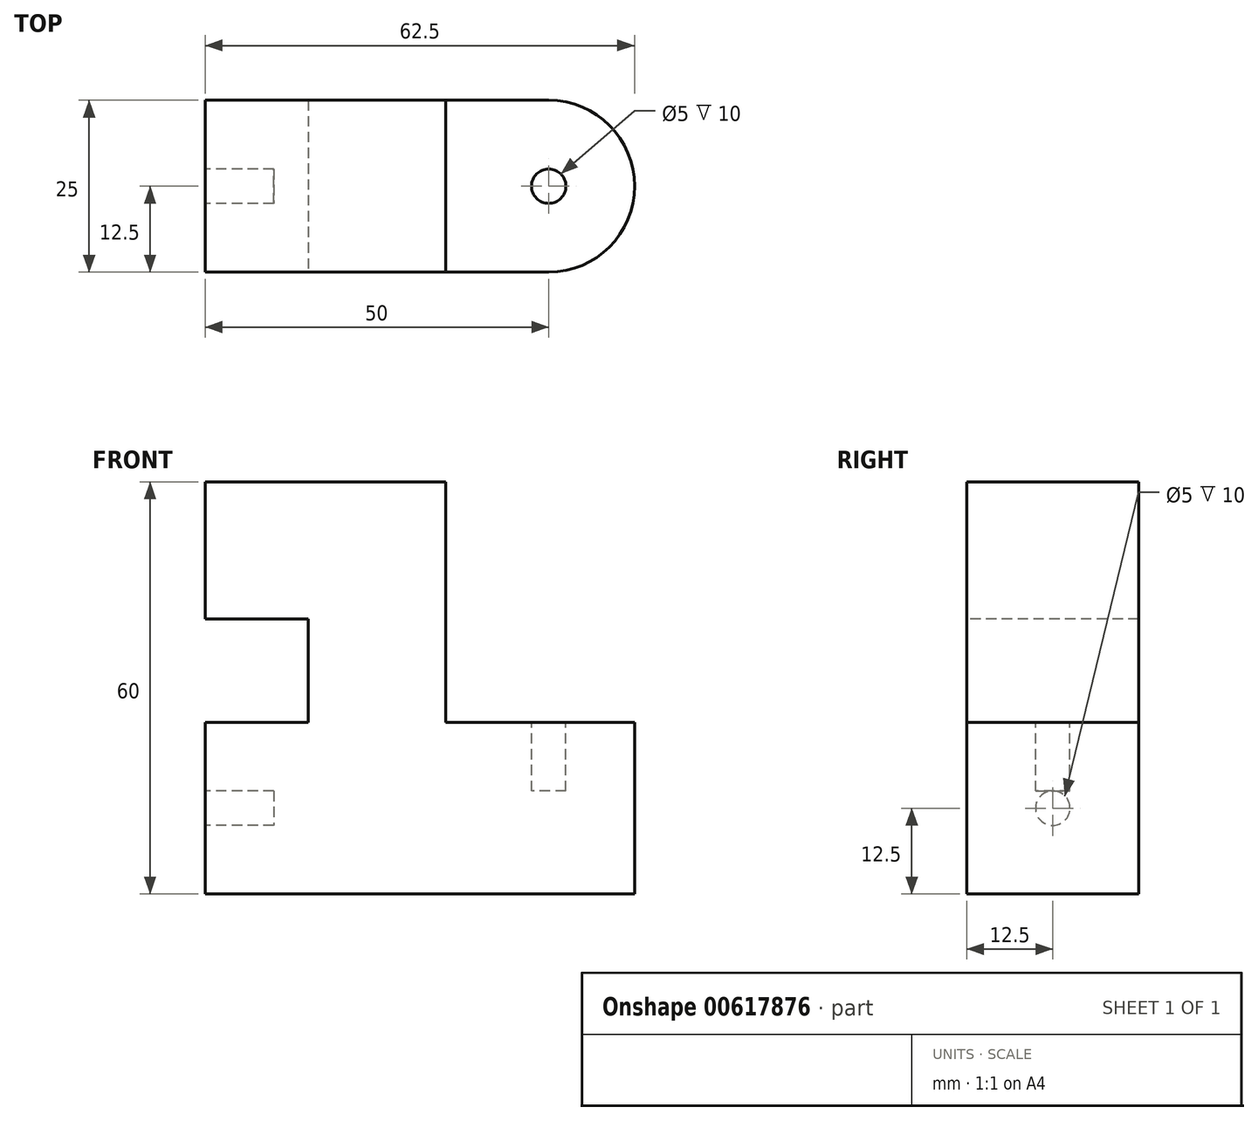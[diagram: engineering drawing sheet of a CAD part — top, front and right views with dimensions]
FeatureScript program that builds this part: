
annotation { "Feature Type Name" : "Feature", "Feature Type Description" : "" }
export const myFeature = defineFeature(function(context is Context, id is Id, definition is map)
    precondition{}
    {
        {
            var Q0;
            Q0=qCreatedBy(makeId("Top.planeOp"),FACE);
            var sketch = newSketch(context, id + "F0", { "sketchPlane" : qUnion([Q0])});
            skLineSegment(sketch, "E0.bottom", {"start": v(0, 0) * mm, "end": v(50, 0) * mm});
            skLineSegment(sketch, "E0.top", {"start": v(0, 25) * mm, "end": v(50, 25) * mm});
            skLineSegment(sketch, "E0.left", {"start": v(0, 0) * mm, "end": v(0, 25) * mm});
            skArc(sketch, "E1", {"start": v(50, 0) * mm, "mid": v(62.5, 12.5) * mm, "end": v(50, 25) * mm});
            skSolve(sketch);
        }
        {
            var Q0;
            Q0=makeQuery(id+"F0.imprint","IMPRINT",FACE,{"disambiguationData":[TD([[makeQuery(id+"F0.imprint","IMPRINT",EDGE,{"derivedFrom":sQuery(id+"F0.wireOp",EDGE,"E0.bottom")}),1.0]])]});
            extrude(context, id + "F1", {"entities" : qUnion([Q0]), "depth" : 25 * mm, "offsetDistance" : 25 * mm});
        }
        {
            var Q0;
            Q0=makeQuery(id+"F1.opExtrude","CAP_FACE",FACE,{"disambiguationData":[OSD([sQuery(id+"F0.wireOp",EDGE,"E0.bottom"),sQuery(id+"F0.wireOp",EDGE,"E0.top"),sQuery(id+"F0.wireOp",EDGE,"E0.left"),sQuery(id+"F0.wireOp",EDGE,"E1")])],"isStart":false});
            var sketch = newSketch(context, id + "F2", { "sketchPlane" : qUnion([Q0])});
            skCircle(sketch, "E2", {"center": v(50, 12.5) * mm, "radius": 2.5 * mm});
            skSolve(sketch);
        }
        {
            var Q0;
            Q0=makeQuery(id+"F2.imprint","IMPRINT",FACE,{"disambiguationData":[TD([[makeQuery(id+"F2.imprint","IMPRINT",EDGE,{"derivedFrom":sQuery(id+"F2.wireOp",EDGE,"E2")}),1.0]])]});
            extrude(context, id + "F3", {"entities" : qUnion([Q0]), "operationType" : NewBodyOperationType.REMOVE, "oppositeDirection" : true, "depth" : 10 * mm, "offsetDistance" : 25 * mm});
        }
        {
            var Q0;
            Q0=makeQuery(id+"F1.opExtrude","SWEPT_FACE",FACE,{"disambiguationData":[OSD([sQuery(id+"F0.wireOp",EDGE,"E0.left")])]});
            var sketch = newSketch(context, id + "F4", { "sketchPlane" : qUnion([Q0])});
            skCircle(sketch, "E3", {"center": v(-12.5, 12.5) * mm, "radius": 2.5 * mm});
            skPoint(sketch, "E3.centerSnap0", {"position": v(-12.5, 25) * mm});
            skPoint(sketch, "E3.centerSnap1", {"position": v(0, 12.5) * mm});
            skSolve(sketch);
        }
        {
            var Q0;
            Q0=makeQuery(id+"F4.imprint","IMPRINT",FACE,{"disambiguationData":[TD([[makeQuery(id+"F4.imprint","IMPRINT",EDGE,{"derivedFrom":sQuery(id+"F4.wireOp",EDGE,"E3")}),1.0]])]});
            extrude(context, id + "F5", {"entities" : qUnion([Q0]), "operationType" : NewBodyOperationType.REMOVE, "oppositeDirection" : true, "depth" : 10 * mm, "offsetDistance" : 25 * mm});
        }
        {
            var Q0;
            Q0=makeQuery(id+"F1.opExtrude","SWEPT_FACE",FACE,{"disambiguationData":[OSD([sQuery(id+"F0.wireOp",EDGE,"E0.bottom")])]});
            var sketch = newSketch(context, id + "F6", { "sketchPlane" : qUnion([Q0])});
            skLineSegment(sketch, "E4", {"start": v(15, 25) * mm, "end": v(15, 40) * mm});
            skLineSegment(sketch, "E5", {"start": v(15, 40) * mm, "end": v(0, 40) * mm});
            skLineSegment(sketch, "E6", {"start": v(0, 40) * mm, "end": v(0, 60) * mm});
            skLineSegment(sketch, "E7", {"start": v(0, 60) * mm, "end": v(35, 60) * mm});
            skLineSegment(sketch, "E8", {"start": v(35, 60) * mm, "end": v(35, 25) * mm});
            skLineSegment(sketch, "E9", {"start": v(35, 25) * mm, "end": v(15, 25) * mm});
            skSolve(sketch);
        }
        {
            var Q0;
            Q0 = qSketchRegion(id + "F6", true);
            extrude(context, id + "F7", {"entities" : qUnion([Q0]), "operationType" : NewBodyOperationType.ADD, "oppositeDirection" : true, "depth" : 25 * mm, "offsetDistance" : 25 * mm});
        }
    });
